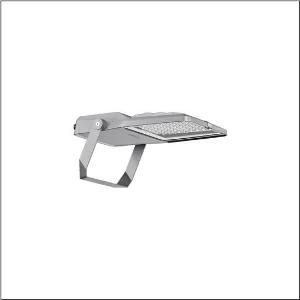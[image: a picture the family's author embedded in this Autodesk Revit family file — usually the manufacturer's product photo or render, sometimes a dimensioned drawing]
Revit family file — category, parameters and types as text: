
# Revit family: floodlight_fl_21_iq_mini___rs12_5xa7772c2b1a_7425
name_source: partatom
category: Lighting Fixtures
units: mm (PartAtom-declared; Revit-internal decimal feet)

## family parameters
Cut with Voids When Loaded = No
Host = Face
Light Source = No
Part Type = Normal
Room Calculation Point = No
Round Connector Dimension = Use Diameter
Shared = No

## types (1)
- --- (1 x LED, 12340 lm, 87.2 W, 3000K)
    Apparent Load = 87 VA
    CIE Flux Codes = 79 92 99 100 100
    Color Rendering = 70
    Color Temperature = 3000K
    Default Elevation = 1800 mm
    Description = Floodlight FL 21 iQ mini, floodlight, primary light control with lens, of PMMA, primary optical cover: protective disc, of toughened safety glass, transparent, light distribution: RS12, light emission: direct distribution, installation type: surface-mounted, LED, High Power LED, rated luminous flux: 12.340lm, luminous efficacy: 142lm/W, light colour: 730, colour temperature: 3000K, control: Street-Remote, Auto-Match, Temp-Guard, Night-Set, Smart-Wire, Desk-Remote (wireless, voltage-free reading and setting of iQ features in the workshop via application-optimized NFC function/RFID function), optimised constant luminous flux control (CLO 2.0), with terminal, 6-pole, mains connection: 220..240V, AC, 50/60Hz, start of lifetime: 87W, end of service life: 92W, reduction: 40W, luminaire housing, of diecast aluminium, powder-coated, Siteco® metallic grey (DB 702S), corrosivity category C5 mid according to DIN EN ISO 12944, sealing non-destructively replaceable, mounting bracket, of steel, galvanised, powder-coated, Siteco® metallic grey (DB 702S), protection rating (complete): IP66, insulation class (complete): insulation class II (safety insulation), certification: CE, ENEC, VDE, protection symbol: D, impact resistance: IK08, permissible operating ambient temperature: -40..+40°C, permissible operating ambient temperature for outdoor applications: -40..+50°C, standard: DIN EN 12944, LABS conformity tested according to VDMA 24364:2018-05, packaging unit: 1 piece

Light Distribution: RS12
    Height = 70 mm
    Lamp = 1 x LED
    Lamp Light Flux = 12340 lm
    Lamp Power = 87.2 W
    Lamp count = 1
    Length = 485 mm
    Luminous efficacy = 142 lm/W
    Manufacturer = Siteco
    ModVariant = No
    Model = 5XA7772C2B1A
    Number of Poles = 1
    OnlyDefault = Yes
    Power Factor = 1
    Product Name = Floodlight FL 21 iQ mini | RS12
    Product group = floodlight | pylon annexe
    ProductGroupID = 6200
    Protection Class = Protection class II
    Protection Degree = IP 66
    RLX_Detail_Level = 1
    RLX_Emergency_Light_Flux = 0 lm
    RLX_Emergency_Type = 0
    RLX_Emergency_Type_DB = No
    RlxData = <blob elided: 91001 chars, md5=6f32a808>
    Socket = socket
    Standby Power = 0 W
    System Light Flux = 12340 lm
    System Power = 87 W
    Type Comments = factory setting: luminous flux: 100 % | dim-lin: 254 | 456 mA
    Type Image = l_1006845.jpg
    URL = http://relux.com
    VarID = @adj_099951
    Voltage = 0 V
    Weight = 0.00 kg
    Width = 337 mm

## geometry (parser evidence)
native form markers: Blend x4, Sweep x13
no freeform markers — native parametric forms only
